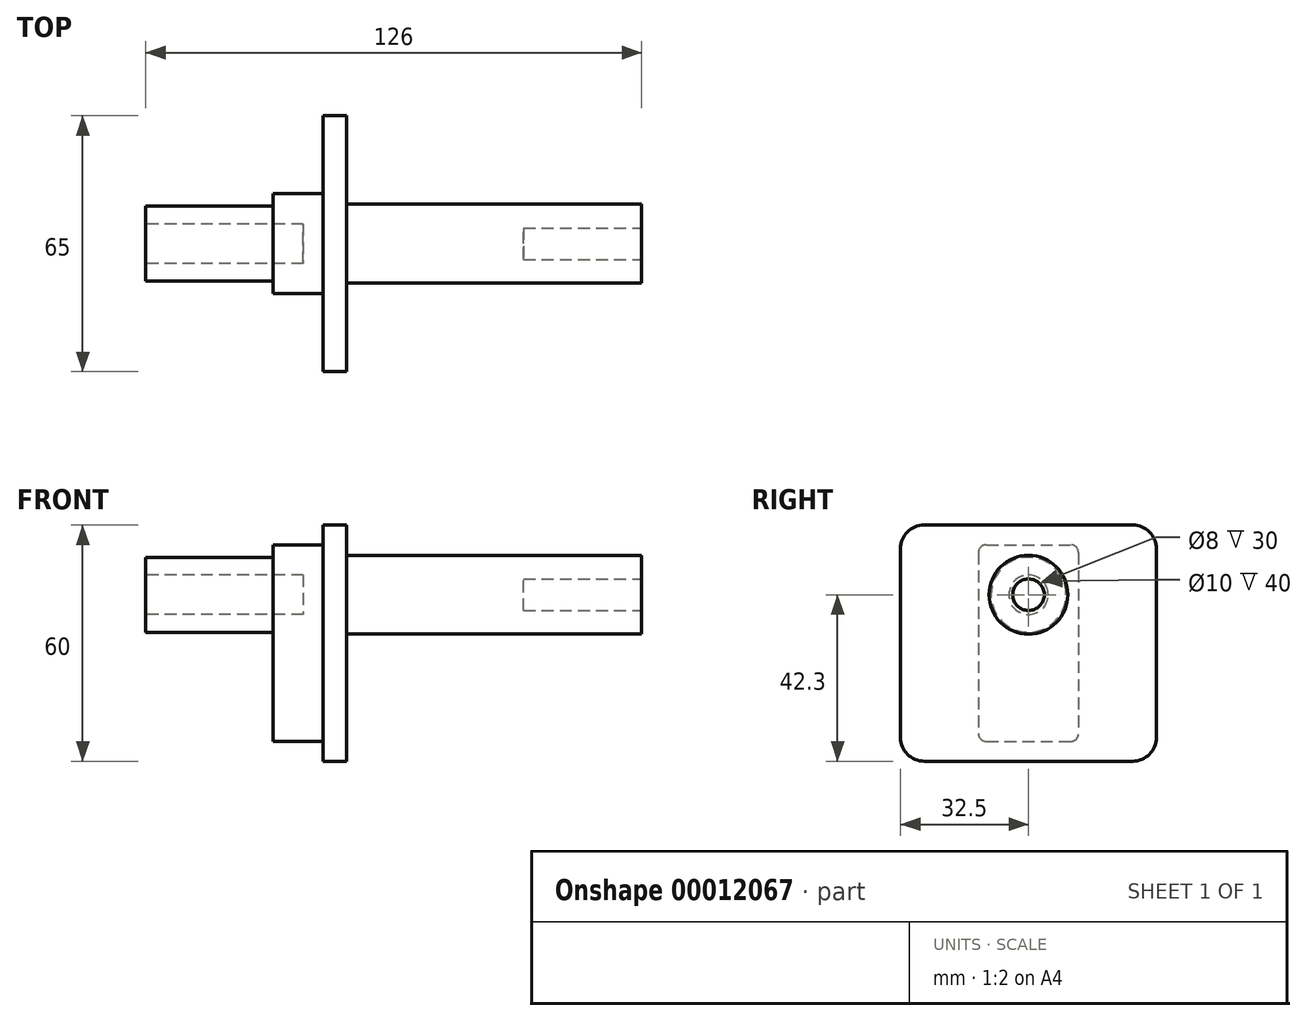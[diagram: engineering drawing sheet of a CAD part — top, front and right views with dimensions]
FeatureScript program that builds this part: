
annotation { "Feature Type Name" : "Feature", "Feature Type Description" : "" }
export const myFeature = defineFeature(function(context is Context, id is Id, definition is map)
    precondition{}
    {
        {
            var Q0;
            Q0=qCreatedBy(makeId("Right.planeOp"),FACE);
            var sketch = newSketch(context, id + "F0", { "sketchPlane" : qUnion([Q0])});
            skCircle(sketch, "E0", {"center": v(0, 0) * mm, "radius": 10 * mm});
            skSolve(sketch);
        }
        {
            var Q0;
            Q0 = qSketchRegion(id + "F0", true);
            extrude(context, id + "F1", {"entities" : qUnion([Q0]), "depth" : 81 * mm, "hasSecondDirection" : true, "secondDirectionOppositeDirection" : true, "secondDirectionDepth" : 45 * mm});
        }
        {
            var Q0;
            Q0=qCreatedBy(makeId("Front.planeOp"),FACE);
            var sketch = newSketch(context, id + "F2", { "sketchPlane" : qUnion([Q0])});
            skLineSegment(sketch, "E1.0", {"start": v(6, 12.23) * mm, "end": v(6, 9.53) * mm});
            skLineSegment(sketch, "E2", {"start": v(6, 9.53) * mm, "end": v(-48.39, 9.52) * mm});
            skLineSegment(sketch, "E3", {"start": v(6, 12.23) * mm, "end": v(-48.39, 12.23) * mm});
            skLineSegment(sketch, "E4", {"start": v(-48.39, 12.23) * mm, "end": v(-48.39, 9.52) * mm});
            skLineSegment(sketch, "E5", {"start": v(0, 0) * mm, "end": v(-50.06, 0) * mm, "construction": true});
            skSolve(sketch);
        }
        {
            var Q0;
            Q0=makeQuery(id+"F2.imprint","IMPRINT",FACE,{"disambiguationData":[TD([[makeQuery(id+"F2.imprint","IMPRINT",EDGE,{"derivedFrom":sQuery(id+"F2.wireOp",EDGE,"E1.0")}),-1.0]])]});
            var Q1;
            Q1=sQuery(id+"F2.wireOp",EDGE,"E5");
            revolve(context, id + "F3", {"operationType" : NewBodyOperationType.REMOVE, "entities" : qUnion([Q0]), "axis" : qUnion([Q1]), "revolveType" : RevolveType.FULL, "oppositeDirection" : true});
        }
        {
            var Q0;
            Q0=qCreatedBy(makeId("Right.planeOp"),FACE);
            var sketch = newSketch(context, id + "F4", { "sketchPlane" : qUnion([Q0])});
            skLineSegment(sketch, "E6.bottom", {"start": v(-10.7, 12.7) * mm, "end": v(10.7, 12.7) * mm});
            skLineSegment(sketch, "E6.top", {"start": v(-10.7, -37.3) * mm, "end": v(10.7, -37.3) * mm});
            skLineSegment(sketch, "E6.left", {"start": v(-12.7, 10.7) * mm, "end": v(-12.7, -35.3) * mm});
            skLineSegment(sketch, "E6.right", {"start": v(12.7, 10.7) * mm, "end": v(12.7, -35.3) * mm});
            skPoint(sketch, "E7.visualSharp", {"position": v(-12.7, 12.7) * mm});
            skArc(sketch, "E7.filletArc", {"start": v(-10.7, 12.7) * mm, "mid": v(-12.11, 12.11) * mm, "end": v(-12.7, 10.7) * mm});
            skPoint(sketch, "E8.visualSharp", {"position": v(12.7, 12.7) * mm});
            skArc(sketch, "E8.filletArc", {"start": v(12.7, 10.7) * mm, "mid": v(12.11, 12.11) * mm, "end": v(10.7, 12.7) * mm});
            skPoint(sketch, "E9.visualSharp", {"position": v(12.7, -37.3) * mm});
            skArc(sketch, "E9.filletArc", {"start": v(10.7, -37.3) * mm, "mid": v(12.11, -36.71) * mm, "end": v(12.7, -35.3) * mm});
            skPoint(sketch, "E10.visualSharp", {"position": v(-12.7, -37.3) * mm});
            skArc(sketch, "E10.filletArc", {"start": v(-12.7, -35.3) * mm, "mid": v(-12.11, -36.71) * mm, "end": v(-10.7, -37.3) * mm});
            skCircle(sketch, "E11", {"center": v(0, 0) * mm, "radius": 9.53 * mm});
            skSolve(sketch);
        }
        {
            var Q0;
            Q0 = qSketchRegion(id + "F4", true);
            extrude(context, id + "F5", {"entities" : qUnion([Q0]), "operationType" : NewBodyOperationType.ADD, "oppositeDirection" : true, "depth" : 12.7 * mm});
        }
        {
            var Q0;
            Q0=qCreatedBy(makeId("Right.planeOp"),FACE);
            var sketch = newSketch(context, id + "F6", { "sketchPlane" : qUnion([Q0])});
            skLineSegment(sketch, "E12.bottom", {"start": v(-26.5, 17.7) * mm, "end": v(26.5, 17.7) * mm});
            skLineSegment(sketch, "E12.top", {"start": v(-26.5, -42.3) * mm, "end": v(26.5, -42.3) * mm});
            skLineSegment(sketch, "E12.left", {"start": v(-32.5, 11.7) * mm, "end": v(-32.5, -36.3) * mm});
            skLineSegment(sketch, "E12.right", {"start": v(32.5, 11.7) * mm, "end": v(32.5, -36.3) * mm});
            skPoint(sketch, "E13.visualSharp", {"position": v(-32.5, 17.7) * mm});
            skArc(sketch, "E13.filletArc", {"start": v(-26.5, 17.7) * mm, "mid": v(-30.74, 15.94) * mm, "end": v(-32.5, 11.7) * mm});
            skPoint(sketch, "E14.visualSharp", {"position": v(32.5, 17.7) * mm});
            skArc(sketch, "E14.filletArc", {"start": v(32.5, 11.7) * mm, "mid": v(30.74, 15.94) * mm, "end": v(26.5, 17.7) * mm});
            skPoint(sketch, "E15.visualSharp", {"position": v(32.5, -42.3) * mm});
            skArc(sketch, "E15.filletArc", {"start": v(26.5, -42.3) * mm, "mid": v(30.74, -40.54) * mm, "end": v(32.5, -36.3) * mm});
            skPoint(sketch, "E16.visualSharp", {"position": v(-32.5, -42.3) * mm});
            skArc(sketch, "E16.filletArc", {"start": v(-32.5, -36.3) * mm, "mid": v(-30.74, -40.54) * mm, "end": v(-26.5, -42.3) * mm});
            skCircle(sketch, "E17", {"center": v(0, 0) * mm, "radius": 9.53 * mm});
            skSolve(sketch);
        }
        {
            var Q0;
            Q0 = qSketchRegion(id + "F6", true);
            extrude(context, id + "F7", {"entities" : qUnion([Q0]), "operationType" : NewBodyOperationType.ADD, "depth" : 6 * mm});
        }
        {
            var Q0;
            Q0=makeQuery(id+"F1.opExtrude","CAP_FACE",FACE,{"disambiguationData":[OSD([sQuery(id+"F0.wireOp",EDGE,"E0")])],"isStart":false});
            var sketch = newSketch(context, id + "F8", { "sketchPlane" : qUnion([Q0])});
            skCircle(sketch, "E18", {"center": v(0, 0) * mm, "radius": 4 * mm});
            skSolve(sketch);
        }
        {
            var Q0;
            Q0 = qSketchRegion(id + "F8", true);
            extrude(context, id + "F9", {"entities" : qUnion([Q0]), "operationType" : NewBodyOperationType.REMOVE, "oppositeDirection" : true, "depth" : 30 * mm});
        }
        {
            var Q0;
            Q0=makeQuery(id+"F1.opExtrude","CAP_FACE",FACE,{"disambiguationData":[OSD([sQuery(id+"F0.wireOp",EDGE,"E0")])],"isStart":true});
            var sketch = newSketch(context, id + "F10", { "sketchPlane" : qUnion([Q0])});
            skCircle(sketch, "E19", {"center": v(0, 0) * mm, "radius": 5 * mm});
            skSolve(sketch);
        }
        {
            var Q0;
            Q0 = qSketchRegion(id + "F10", true);
            extrude(context, id + "F11", {"entities" : qUnion([Q0]), "operationType" : NewBodyOperationType.REMOVE, "oppositeDirection" : true, "depth" : 40 * mm});
        }
    });
